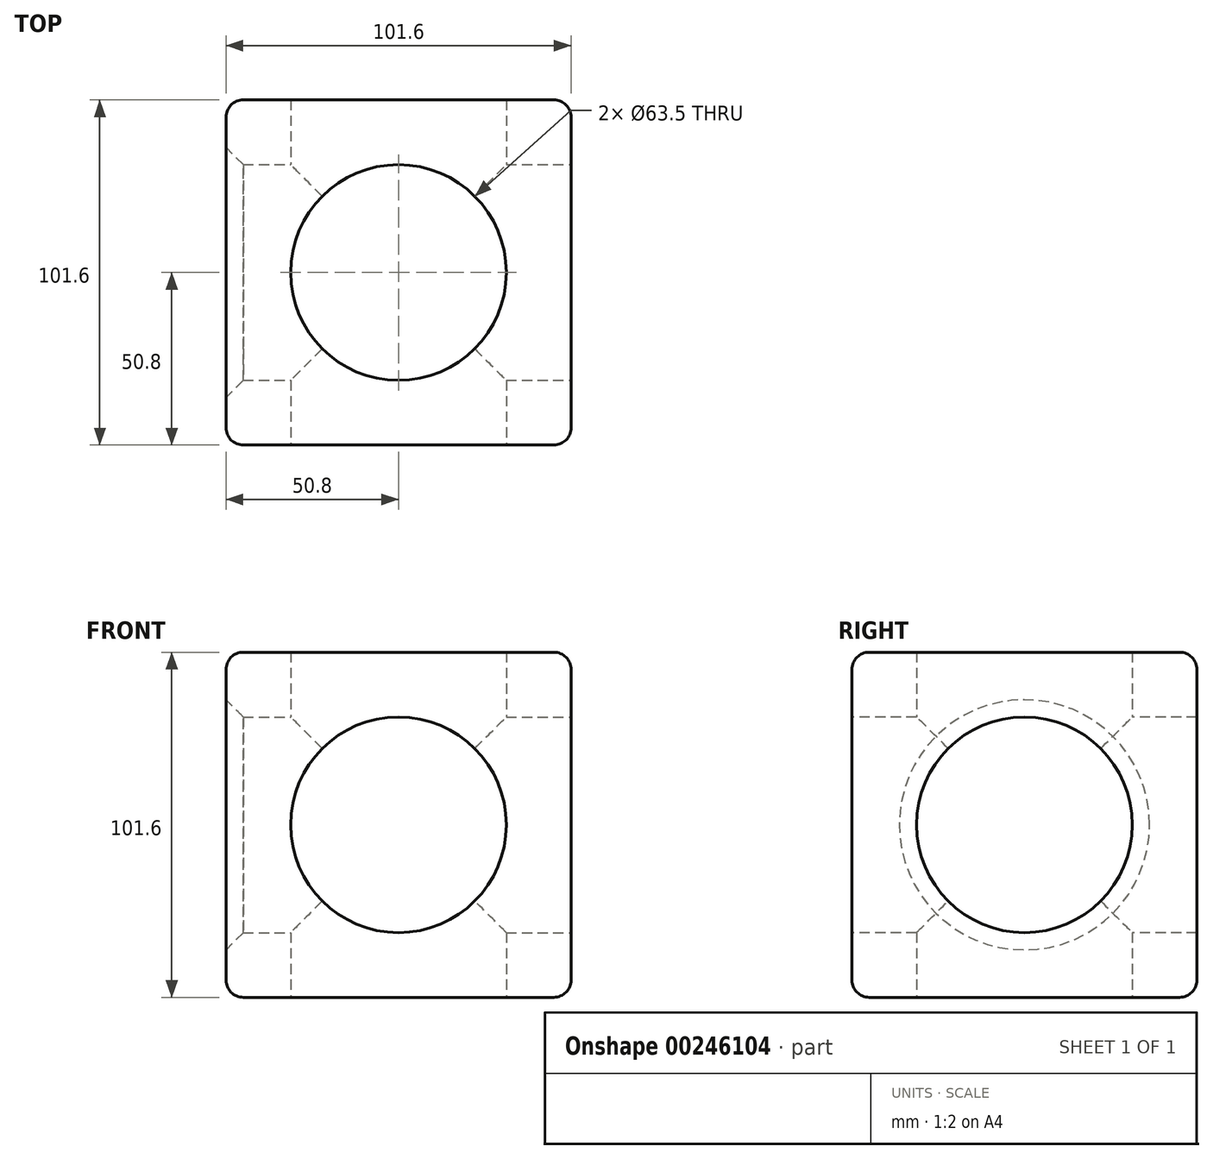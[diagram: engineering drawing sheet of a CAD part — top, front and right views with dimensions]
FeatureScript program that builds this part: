
annotation { "Feature Type Name" : "Feature", "Feature Type Description" : "" }
export const myFeature = defineFeature(function(context is Context, id is Id, definition is map)
    precondition{}
    {
        {
            var Q0;
            Q0=qCreatedBy(makeId("Top.planeOp"),FACE);
            var sketch = newSketch(context, id + "F0", { "sketchPlane" : qUnion([Q0])});
            skLineSegment(sketch, "E0", {"start": v(0, 0) * mm, "end": v(0, 101.6) * mm});
            skLineSegment(sketch, "E1", {"start": v(0, 101.6) * mm, "end": v(101.6, 101.6) * mm});
            skLineSegment(sketch, "E2", {"start": v(101.6, 101.6) * mm, "end": v(101.6, 0) * mm});
            skLineSegment(sketch, "E3", {"start": v(0, 0) * mm, "end": v(101.6, 0) * mm});
            skSolve(sketch);
        }
        {
            var Q0;
            Q0=makeQuery(id+"F0.imprint","IMPRINT",FACE,{"disambiguationData":[TD([[makeQuery(id+"F0.imprint","IMPRINT",EDGE,{"derivedFrom":sQuery(id+"F0.wireOp",EDGE,"E0")}),-1.0]])]});
            extrude(context, id + "F1", {"entities" : qUnion([Q0]), "depth" : 101.6 * mm});
        }
        {
            var Q0;
            Q0=makeQuery(id+"F1.opExtrude","SWEPT_FACE",FACE,{"disambiguationData":[OSD([sQuery(id+"F0.wireOp",EDGE,"E2")])]});
            var sketch = newSketch(context, id + "F2", { "sketchPlane" : qUnion([Q0])});
            skCircle(sketch, "E4", {"center": v(50.8, 50.8) * mm, "radius": 31.75 * mm});
            skSolve(sketch);
        }
        {
            var Q0;
            Q0 = qSketchRegion(id + "F2", true);
            var Q1;
            Q1=makeQuery(id+"F1.opExtrude","SWEPT_FACE",FACE,{"disambiguationData":[OSD([sQuery(id+"F0.wireOp",EDGE,"E0")])]});
            extrude(context, id + "F3", {"entities" : qUnion([Q0, Q1]), "operationType" : NewBodyOperationType.REMOVE, "oppositeDirection" : true, "depth" : 101.6 * mm});
        }
        {
            var Q0;
            Q0=makeQuery(id+"F1.opExtrude","SWEPT_FACE",FACE,{"disambiguationData":[OSD([sQuery(id+"F0.wireOp",EDGE,"E3")])]});
            var sketch = newSketch(context, id + "F4", { "sketchPlane" : qUnion([Q0])});
            skCircle(sketch, "E5", {"center": v(50.8, 50.8) * mm, "radius": 31.75 * mm});
            skSolve(sketch);
        }
        {
            var Q0;
            Q0 = qSketchRegion(id + "F4", true);
            extrude(context, id + "F5", {"entities" : qUnion([Q0]), "operationType" : NewBodyOperationType.REMOVE, "oppositeDirection" : true, "depth" : 101.6 * mm});
        }
        {
            var Q0;
            Q0=makeQuery(id+"F1.opExtrude","CAP_FACE",FACE,{"disambiguationData":[OSD([sQuery(id+"F0.wireOp",EDGE,"E0"),sQuery(id+"F0.wireOp",EDGE,"E1"),sQuery(id+"F0.wireOp",EDGE,"E2"),sQuery(id+"F0.wireOp",EDGE,"E3")])],"isStart":true});
            var sketch = newSketch(context, id + "F6", { "sketchPlane" : qUnion([Q0])});
            skCircle(sketch, "E6", {"center": v(50.8, -50.8) * mm, "radius": 31.75 * mm});
            skSolve(sketch);
        }
        {
            var Q0;
            Q0=makeQuery(id+"F6.imprint","IMPRINT",FACE,{"disambiguationData":[TD([[makeQuery(id+"F6.imprint","IMPRINT",EDGE,{"derivedFrom":sQuery(id+"F6.wireOp",EDGE,"E6")}),1.0]])]});
            extrude(context, id + "F7", {"entities" : qUnion([Q0]), "operationType" : NewBodyOperationType.REMOVE, "oppositeDirection" : true, "depth" : 101.6 * mm});
        }
        {
            var Q0;
            Q0=makeQuery(id+"F1.opExtrude","CAP_EDGE",EDGE,{"disambiguationData":[OSD([sQuery(id+"F0.wireOp",EDGE,"E3")])],"isStart":false});
            var Q1;
            Q1=makeQuery(id+"F1.opExtrude","CAP_EDGE",EDGE,{"disambiguationData":[OSD([sQuery(id+"F0.wireOp",EDGE,"E2")])],"isStart":false});
            var Q2;
            Q2=makeQuery(id+"F1.opExtrude","CAP_EDGE",EDGE,{"disambiguationData":[OSD([sQuery(id+"F0.wireOp",EDGE,"E1")])],"isStart":false});
            var Q3;
            Q3=makeQuery(id+"F1.opExtrude","CAP_EDGE",EDGE,{"disambiguationData":[OSD([sQuery(id+"F0.wireOp",EDGE,"E0")])],"isStart":false});
            var Q4;
            Q4=makeQuery(id+"F1.opExtrude","SWEPT_EDGE",EDGE,{"disambiguationData":[OSD([sQuery(id+"F0.wireOp",EDGE,"E1"),sQuery(id+"F0.wireOp",EDGE,"E2")])]});
            var Q5;
            Q5=makeQuery(id+"F1.opExtrude","SWEPT_EDGE",EDGE,{"disambiguationData":[OSD([sQuery(id+"F0.wireOp",EDGE,"E2"),sQuery(id+"F0.wireOp",EDGE,"E3")])]});
            var Q6;
            Q6=makeQuery(id+"F1.opExtrude","CAP_EDGE",EDGE,{"disambiguationData":[OSD([sQuery(id+"F0.wireOp",EDGE,"E2")])],"isStart":true});
            var Q7;
            Q7=makeQuery(id+"F1.opExtrude","CAP_EDGE",EDGE,{"disambiguationData":[OSD([sQuery(id+"F0.wireOp",EDGE,"E1")])],"isStart":true});
            var Q8;
            Q8=makeQuery(id+"F1.opExtrude","SWEPT_EDGE",EDGE,{"disambiguationData":[OSD([sQuery(id+"F0.wireOp",EDGE,"E0"),sQuery(id+"F0.wireOp",EDGE,"E1")])]});
            var Q9;
            Q9=makeQuery(id+"F1.opExtrude","CAP_EDGE",EDGE,{"disambiguationData":[OSD([sQuery(id+"F0.wireOp",EDGE,"E3")])],"isStart":true});
            var Q10;
            Q10=makeQuery(id+"F1.opExtrude","SWEPT_EDGE",EDGE,{"disambiguationData":[OSD([sQuery(id+"F0.wireOp",EDGE,"E0"),sQuery(id+"F0.wireOp",EDGE,"E3")])]});
            fillet(context, id + "F8", {"entities" : qUnion([Q0, Q1, Q2, Q3, Q4, Q5, Q6, Q7, Q8, Q9, Q10]), "radius" : 5.08 * mm, "tangentPropagation" : true, "allowEdgeOverflow" : false});
        }
        {
            var Q0;
            Q0=makeQuery(id+"F1.opExtrude","CAP_EDGE",EDGE,{"disambiguationData":[OSD([sQuery(id+"F0.wireOp",EDGE,"E0")])],"isStart":true});
            fillet(context, id + "F9", {"entities" : qUnion([Q0]), "radius" : 5.08 * mm, "tangentPropagation" : true, "allowEdgeOverflow" : false});
        }
        {
            var Q0;
            Q0=makeQuery(id+"F3.boolean.opBoolean","COPY",EDGE,{"derivedFrom":makeQuery(id+"F3.opExtrude","CAP_EDGE",EDGE,{"disambiguationData":[OSD([sQuery(id+"F2.wireOp",EDGE,"E4")])],"isStart":true})});
            var Q1;
            Q1=makeQuery(id+"F7.boolean.opBoolean","COPY",EDGE,{"derivedFrom":makeQuery(id+"F7.opExtrude","CAP_EDGE",EDGE,{"disambiguationData":[OSD([sQuery(id+"F6.wireOp",EDGE,"E6")])],"isStart":true})});
            var Q2;
            Q2=makeQuery(id+"F5.boolean.opBoolean","COPY",EDGE,{"derivedFrom":makeQuery(id+"F5.opExtrude","CAP_EDGE",EDGE,{"disambiguationData":[OSD([sQuery(id+"F4.wireOp",EDGE,"E5")])],"isStart":true})});
            var Q3;
            Q3=makeQuery(id+"F7.boolean.opBoolean","COPY",EDGE,{"derivedFrom":makeQuery(id+"F7.opExtrude","CAP_EDGE",EDGE,{"disambiguationData":[OSD([sQuery(id+"F6.wireOp",EDGE,"E6")])],"isStart":false})});
            var Q4;
            Q4=makeQuery(id+"F5.boolean.opBoolean","COPY",EDGE,{"derivedFrom":makeQuery(id+"F5.opExtrude","CAP_EDGE",EDGE,{"disambiguationData":[OSD([sQuery(id+"F4.wireOp",EDGE,"E5")])],"isStart":false})});
            var Q5;
            {var subQ0=sQuery(id+"F0.wireOp",EDGE,"E0");Q5=makeQuery(id+"F3.boolean.opBoolean","INTERSECT",EDGE,{"derivedFrom":[makeQuery(id+"F1.opExtrude","SWEPT_FACE",FACE,{"disambiguationData":[OSD([subQ0])]}),makeQuery(id+"F3.opExtrude","CAP_FACE",FACE,{"disambiguationData":[OSD([subQ0])],"isStart":true})]});}
            chamfer(context, id + "F10", {"entities" : qUnion([Q0, Q1, Q2, Q3, Q4, Q5]), "width" : 5.08 * mm, "tangentPropagation" : true});
        }
    });
